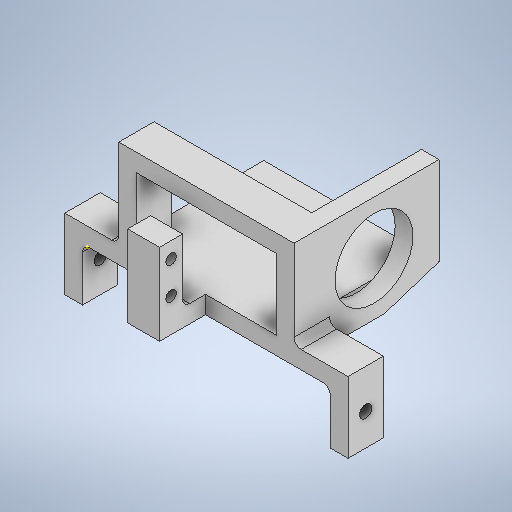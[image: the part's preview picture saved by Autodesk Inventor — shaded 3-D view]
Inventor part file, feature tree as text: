
AUTODESK INVENTOR PART (.ipt)
format: ipt  version: 2025.2 (Build 292293000, 293)  size: 503,808 bytes
history: native  units: mm
features: extrude x21, sketch x20, thread x4, mirror x1, pattern_linear x1, fillet x1
ambient origin geometry x8: Origin, YZ Plane, XZ Plane, XY Plane, X Axis, Y Axis, Z Axis, Center Point
bodies: Solid1 (feature_tree)
feature tree (48):
  sketch  "Sketch1"  dims[d0=70.0mm d1=10.0mm]
  extrude  "Extrusion1"  Depth=10.0mm
  extrude  "Extrusion2"  Depth=5.0mm
  extrude  "Extrusion3"  Depth=5.0mm TaperAngle=0.0deg
  extrude  "Extrusion4"  Depth=19.75mm
  extrude  "Extrusion5"  Depth=5.0mm
  mirror  "Mirror1"
  pattern_linear  "Rectangular Pattern1"  Count1=2  [1 undecoded]
  sketch  "Sketch5"  dims[d10=5.0mm d11=5.0mm]
  sketch  "Sketch6"  dims[d12=25.0mm d13=0.0mm]
  extrude  "Extrusion6"  Depth=25.0mm
  extrude  "Extrusion7"  Depth=5.5mm TaperAngle=0.0deg
  extrude  "Extrusion8"  Depth=10.5mm
  extrude  "Extrusion9"  Depth=9.0mm
  extrude  "Extrusion10"  Depth=13.0mm TaperAngle=0.0deg
  thread  "Thread1"  [1 undecoded]
  thread  "Thread2"  [1 undecoded]
  extrude  "Extrusion12"  Depth=3.0mm
  extrude  "Extrusion13"  Depth=9.0mm TaperAngle=0.0deg
  extrude  "Extrusion14"  Depth=20.0mm TaperAngle=0.0deg
  extrude  "Extrusion15"  Depth=2.5mm TaperAngle=0.0deg
  extrude  "Extrusion16"  Depth=31.0mm TaperAngle=0.0deg
  sketch  "Sketch16"  dims[d41=10.0mm d42=0.0mm d43=9.0mm d44=0.0mm]
  extrude  "Extrusion17"  Depth=22.0mm
  extrude  "Extrusion18"  Depth=31.0mm TaperAngle=0.0deg
  extrude  "Extrusion19"  Depth=11.0mm TaperAngle=0.0deg
  extrude  "Extrusion20"  Depth=11.0mm TaperAngle=0.0deg
  extrude  "Extrusion21"  Depth=44.5mm TaperAngle=0.0deg
  extrude  "Extrusion22"  Depth=5.0mm TaperAngle=0.0deg
  fillet  "Fillet4"  Radius=2.0mm
  thread  "Thread3"  [1 undecoded]
  thread  "Thread4"  [1 undecoded]
  sketch  "Sketch2"  dims[d2=5.0mm d3=5.0mm]
  sketch  "Sketch3"  dims[d4=15.0mm d5=0.0mm d6=5.0mm d7=0.0mm]
  sketch  "Sketch4"  dims[d8=19.75mm d9=19.75mm]
  sketch  "Sketch7"  dims[d14=5.0mm]
  sketch  "Sketch8"  dims[d15=5.0mm d16=20.0mm]
  sketch  "Sketch9"  dims[d17=25.0mm d18=0.0mm d20=6.0mm]
  sketch  "Sketch11"  dims[d21=3.5mm d22=5.5mm d23=0.0mm]
  sketch  "Sketch12"  dims[d24=20.0mm d26=64.5mm d28=10.5mm]
  sketch  "Sketch13"  dims[d29=9.0mm d30=9.0mm]
  sketch  "Sketch14"  dims[d31=6.0mm d32=0.0mm d33=13.0mm d34=0.0mm d35=13.0mm d36=0.0mm d37=18.0mm d38=0.0mm]
  sketch  "Sketch15"  dims[d39=3.0mm d40=3.0mm]
  sketch  "Sketch17"  dims[d45=9.0mm d46=0.0mm d49=20.0mm d50=0.0mm]
  sketch  "Sketch18"  dims[d51=20.0mm d52=0.0mm d53=2.5mm d54=0.0mm]
  sketch  "Sketch19"  dims[d55=2.12mm d56=0.0mm d57=31.0mm d58=0.0mm]
  sketch  "Sketch20"  dims[d59=12.62mm d60=22.0mm]
  sketch  "Sketch21"  dims[d61=31.0mm d62=0.0mm d63=31.0mm d64=0.0mm d65=11.0mm d66=0.0mm d67=11.0mm d68=0.0mm d71=44.5mm d72=0.0mm d73=5.0mm d74=0.0mm d76=2.0mm d77=5.0mm d78=0.0mm d79=5.0mm d80=0.0mm d75=0.0mm]
note: 5 required parameter values undecoded (feature->parameter linkage not recoverable at this tier; creation-order binding heuristic only, values carry confidence <= 0.55)
